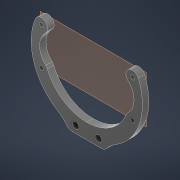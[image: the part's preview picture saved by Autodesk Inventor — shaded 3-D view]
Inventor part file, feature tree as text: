
AUTODESK INVENTOR PART (.ipt)
format: ipt  version: 2021 (Build 250183000, 183)  size: 178,176 bytes
history: native  units: mm
features: other x7, reference x3, plane x1, extrude x1, sketch x1
ambient origin geometry x8: Origin, YZ Plane, XZ Plane, XY Plane, X Axis, Y Axis, Z Axis, Center Point
bodies: Solid1 (feature_tree)
feature tree (13):
  plane  "Work Plane1"
  extrude  "Extrusion1"  Depth=20.0mm
  sketch  "Sketch1"  dims[d0=6.0mm d9=20.0mm d11=17.5mm d12=10.0mm d14=10.0mm d16=15.9004mm d17=8.903582mm d19=8.903582mm d20=14.535529mm d21=13.8mm d22=3.1mm d24=9.979422mm d25=19.958843mm d26=6.2mm d29=14.535529mm d30=3.0mm d31=0.0mm d32=24.0mm d33=26.0mm d34=0.2mm d37=0.2mm]
  reference  "Reference1"
  reference  "Reference2"
  reference  "Reference3"
  parser-record x1  (decoder bookkeeping rows leaked as tree rows — omitted from the tree; the rows remain in map.json)
  other  "mount_hcsr04.iam"
  other  "hcsr04:1"
  other  "Board"
  other  "Transducer:2"
  other  "TransducerBody:1"
  other  "Transducer:1"
note: 1 file-system path scrubbed to <path> (originals preserved in map.json)
